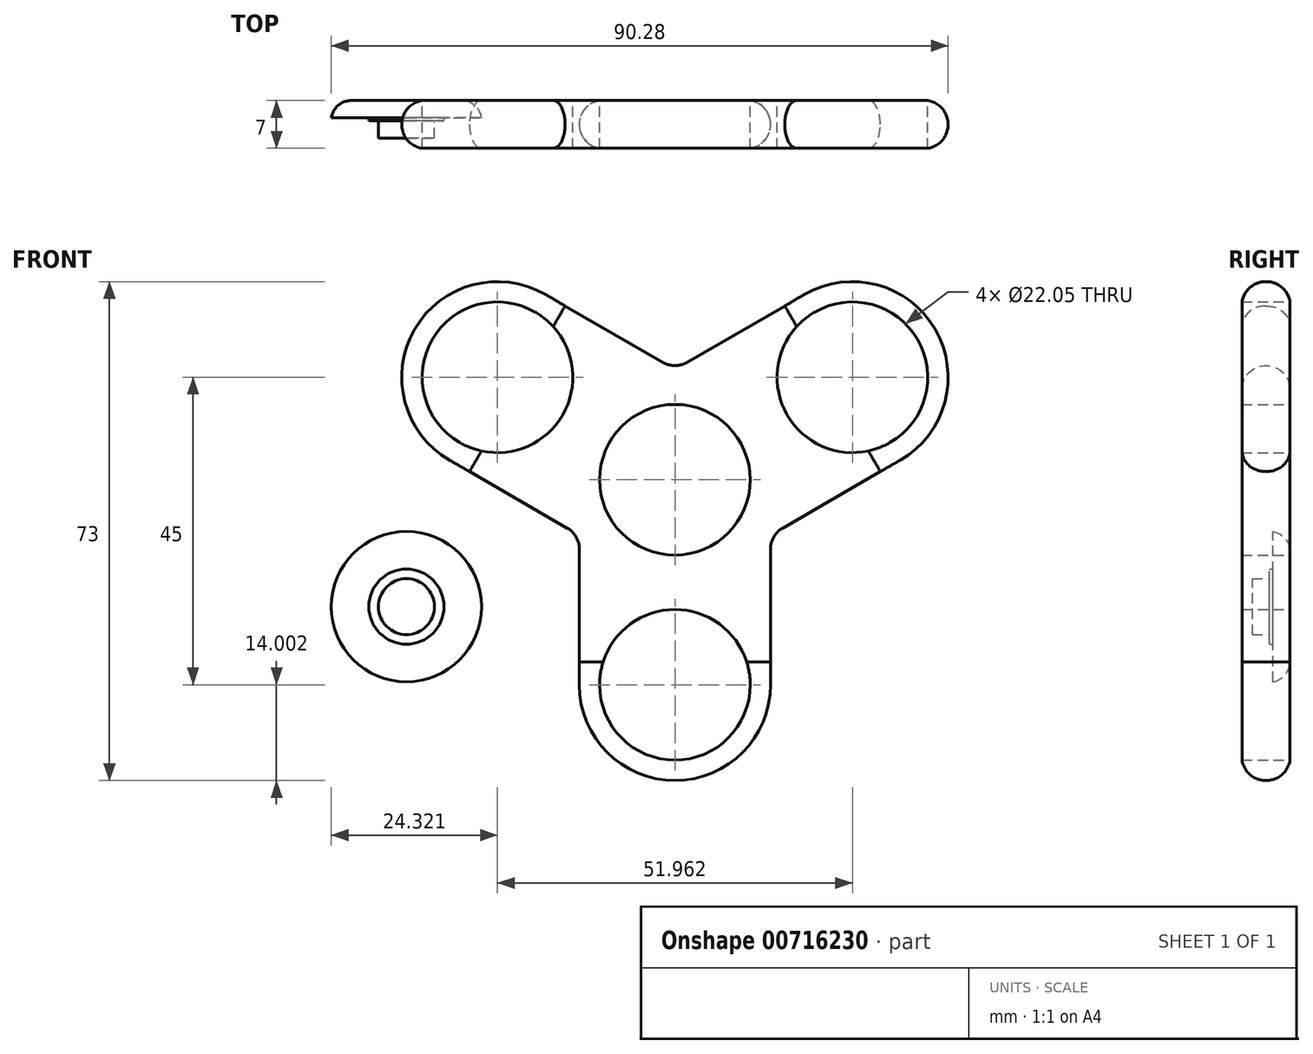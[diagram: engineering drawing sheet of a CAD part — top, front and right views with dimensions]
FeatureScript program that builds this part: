
annotation { "Feature Type Name" : "Feature", "Feature Type Description" : "" }
export const myFeature = defineFeature(function(context is Context, id is Id, definition is map)
    precondition{}
    {
        {
            var Q0;
            Q0=qCreatedBy(makeId("Front.planeOp"),FACE);
            var sketch = newSketch(context, id + "F0", { "sketchPlane" : qUnion([Q0])});
            skLineSegment(sketch, "E0.bottom", {"start": v(-7.75, 14.35) * mm, "end": v(20.25, 14.35) * mm});
            skLineSegment(sketch, "E0.top", {"start": v(-7.75, -15.65) * mm, "end": v(20.25, -15.65) * mm});
            skLineSegment(sketch, "E0.left", {"start": v(-7.75, 14.35) * mm, "end": v(-7.75, -15.65) * mm});
            skLineSegment(sketch, "E0.right", {"start": v(20.25, 14.35) * mm, "end": v(20.25, -15.65) * mm});
            skCircle(sketch, "E1", {"center": v(6.25, 14.35) * mm, "radius": 14 * mm});
            skCircle(sketch, "E2", {"center": v(6.25, 14.35) * mm, "radius": 11.03 * mm});
            skCircle(sketch, "E3", {"center": v(6.25, -15.65) * mm, "radius": 14 * mm});
            skCircle(sketch, "E4", {"center": v(6.25, -15.65) * mm, "radius": 11.03 * mm});
            skSolve(sketch);
        }
        {
            var Q0;
            {var subQ1=sQuery(id+"F0.wireOp",EDGE,"E0.bottom");var subQ3=sQuery(id+"F0.wireOp",EDGE,"E2");var subQ4=makeQuery(id+"F0.imprint","INTERSECT",VERTEX,{"disambiguationData":[OD(0.0)],"derivedFrom":[subQ1,subQ3]});Q0=makeQuery(id+"F0.imprint","IMPRINT",FACE,{"disambiguationData":[TD([[makeQuery(id+"F0.imprint","IMPRINT",EDGE,{"disambiguationData":[TD([[subQ4,1.0]])],"derivedFrom":subQ3}),-1.0]])]});}
            var Q1;
            {var subQ1=sQuery(id+"F0.wireOp",EDGE,"E0.top");var subQ3=sQuery(id+"F0.wireOp",EDGE,"E4");var subQ4=makeQuery(id+"F0.imprint","INTERSECT",VERTEX,{"disambiguationData":[OD(0.0)],"derivedFrom":[subQ1,subQ3]});Q1=makeQuery(id+"F0.imprint","IMPRINT",FACE,{"disambiguationData":[TD([[makeQuery(id+"F0.imprint","IMPRINT",EDGE,{"disambiguationData":[TD([[subQ4,-1.0]])],"derivedFrom":subQ3}),-1.0]])]});}
            var Q2;
            {var subQ1=sQuery(id+"F0.wireOp",EDGE,"E0.bottom");var subQ3=sQuery(id+"F0.wireOp",EDGE,"E2");var subQ4=makeQuery(id+"F0.imprint","INTERSECT",VERTEX,{"disambiguationData":[OD(0.0)],"derivedFrom":[subQ1,subQ3]});Q2=makeQuery(id+"F0.imprint","IMPRINT",FACE,{"disambiguationData":[TD([[makeQuery(id+"F0.imprint","IMPRINT",EDGE,{"disambiguationData":[TD([[subQ4,-1.0]])],"derivedFrom":subQ3}),-1.0]])]});}
            var Q3;
            {var subQ1=sQuery(id+"F0.wireOp",EDGE,"E0.top");var subQ3=sQuery(id+"F0.wireOp",EDGE,"E4");var subQ4=makeQuery(id+"F0.imprint","INTERSECT",VERTEX,{"disambiguationData":[OD(0.0)],"derivedFrom":[subQ1,subQ3]});Q3=makeQuery(id+"F0.imprint","IMPRINT",FACE,{"disambiguationData":[TD([[makeQuery(id+"F0.imprint","IMPRINT",EDGE,{"disambiguationData":[TD([[subQ4,1.0]])],"derivedFrom":subQ3}),-1.0]])]});}
            var Q4;
            {var subQ0=sQuery(id+"F0.wireOp",EDGE,"E0.left");Q4=makeQuery(id+"F0.imprint","IMPRINT",FACE,{"disambiguationData":[TD([[makeQuery(id+"F0.imprint","IMPRINT",EDGE,{"derivedFrom":subQ0}),1.0]])]});}
            extrude(context, id + "F1", {"entities" : qUnion([Q0, Q1, Q2, Q3, Q4]), "depth" : 7 * mm, "offsetDistance" : 25 * mm});
        }
        {
            var Q0;
            Q0=makeQuery(id+"F1.opExtrude","SWEPT_BODY",BODY,{"disambiguationData":[OSD([sQuery(id+"F0.wireOp",EDGE,"E0.left"),sQuery(id+"F0.wireOp",EDGE,"E0.right"),sQuery(id+"F0.wireOp",EDGE,"E1"),sQuery(id+"F0.wireOp",EDGE,"E2"),sQuery(id+"F0.wireOp",EDGE,"E3"),sQuery(id+"F0.wireOp",EDGE,"E4")])]});
            var Q1;
            Q1=makeQuery(id+"F1.opExtrude","SWEPT_FACE",FACE,{"disambiguationData":[OSD([sQuery(id+"F0.wireOp",EDGE,"E1")])]});
            circularPattern(context, id + "F2", {"operationType" : NewBodyOperationType.ADD, "entities" : qUnion([Q0]), "axis" : qUnion([Q1]), "angle" : 360 * degree, "instanceCount" : 3, "equalSpace" : true});
        }
        {
            var Q0;
            Q0=qCreatedBy(makeId("Front.planeOp"),FACE);
            var sketch = newSketch(context, id + "F3", { "sketchPlane" : qUnion([Q0])});
            skCircle(sketch, "E5", {"center": v(-33.05, -4.22) * mm, "radius": 11 * mm});
            skCircle(sketch, "E6", {"center": v(-33.05, -4.22) * mm, "radius": 5.5 * mm});
            skCircle(sketch, "E7", {"center": v(-33.05, -4.22) * mm, "radius": 4.1 * mm});
            skSolve(sketch);
        }
        {
            var Q0;
            Q0 = qSketchRegion(id + "F3", true);
            extrude(context, id + "F4", {"entities" : qUnion([Q0]), "depth" : 2.5 * mm, "offsetDistance" : 25 * mm});
        }
        {
            var Q0;
            Q0=makeQuery(id+"F3.imprint","IMPRINT",FACE,{"disambiguationData":[TD([[makeQuery(id+"F3.imprint","IMPRINT",EDGE,{"derivedFrom":sQuery(id+"F3.wireOp",EDGE,"E6")}),1.0]])]});
            extrude(context, id + "F5", {"entities" : qUnion([Q0]), "operationType" : NewBodyOperationType.ADD, "depth" : 3 * mm, "offsetDistance" : 25 * mm});
        }
        {
            var Q0;
            Q0=makeQuery(id+"F3.imprint","IMPRINT",FACE,{"disambiguationData":[TD([[makeQuery(id+"F3.imprint","IMPRINT",EDGE,{"derivedFrom":sQuery(id+"F3.wireOp",EDGE,"E7")}),1.0]])]});
            extrude(context, id + "F6", {"entities" : qUnion([Q0]), "operationType" : NewBodyOperationType.ADD, "depth" : 5.5 * mm, "offsetDistance" : 25 * mm});
        }
        {
            var Q0;
            Q0=makeQuery(id+"F1.opExtrude","CAP_EDGE",EDGE,{"disambiguationData":[OSD([sQuery(id+"F0.wireOp",EDGE,"E0.right")])],"isStart":false});
            var Q1;
            Q1=makeQuery(id+"F2.opPattern","COPY",EDGE,{"derivedFrom":makeQuery(id+"F1.opExtrude","CAP_EDGE",EDGE,{"disambiguationData":[OSD([sQuery(id+"F0.wireOp",EDGE,"E0.right")])],"isStart":false}),"instanceName":"1"});
            var Q2;
            Q2=makeQuery(id+"F2.opPattern","COPY",EDGE,{"derivedFrom":makeQuery(id+"F1.opExtrude","CAP_EDGE",EDGE,{"disambiguationData":[OSD([sQuery(id+"F0.wireOp",EDGE,"E0.right")])],"isStart":false}),"instanceName":"2"});
            var Q3;
            Q3=makeQuery(id+"F2.opPattern","COPY",EDGE,{"derivedFrom":makeQuery(id+"F1.opExtrude","CAP_EDGE",EDGE,{"disambiguationData":[OSD([sQuery(id+"F0.wireOp",EDGE,"E0.left")])],"isStart":true}),"instanceName":"2"});
            var Q4;
            Q4=makeQuery(id+"F2.opPattern","COPY",EDGE,{"derivedFrom":makeQuery(id+"F1.opExtrude","CAP_EDGE",EDGE,{"disambiguationData":[OSD([sQuery(id+"F0.wireOp",EDGE,"E0.left")])],"isStart":true}),"instanceName":"1"});
            var Q5;
            Q5=makeQuery(id+"F1.opExtrude","CAP_EDGE",EDGE,{"disambiguationData":[OSD([sQuery(id+"F0.wireOp",EDGE,"E0.left")])],"isStart":true});
            var Q6;
            Q6=makeQuery(id+"F2.boolean.opBoolean","INTERSECT",EDGE,{"derivedFrom":[makeQuery(id+"F1.opExtrude","SWEPT_FACE",FACE,{"disambiguationData":[OSD([sQuery(id+"F0.wireOp",EDGE,"E0.left")])]}),makeQuery(id+"F2.opPattern","COPY",FACE,{"derivedFrom":makeQuery(id+"F1.opExtrude","SWEPT_FACE",FACE,{"disambiguationData":[OSD([sQuery(id+"F0.wireOp",EDGE,"E0.right")])]}),"instanceName":"1"})]});
            var Q7;
            Q7=makeQuery(id+"F2.boolean.opBoolean","INTERSECT",EDGE,{"derivedFrom":[makeQuery(id+"F1.opExtrude","SWEPT_FACE",FACE,{"disambiguationData":[OSD([sQuery(id+"F0.wireOp",EDGE,"E0.right")])]}),makeQuery(id+"F2.opPattern","COPY",FACE,{"derivedFrom":makeQuery(id+"F1.opExtrude","SWEPT_FACE",FACE,{"disambiguationData":[OSD([sQuery(id+"F0.wireOp",EDGE,"E0.left")])]}),"instanceName":"2"})]});
            var Q8;
            Q8=makeQuery(id+"F2.boolean.opBoolean","INTERSECT",EDGE,{"derivedFrom":[makeQuery(id+"F2.opPattern","COPY",FACE,{"derivedFrom":makeQuery(id+"F1.opExtrude","SWEPT_FACE",FACE,{"disambiguationData":[OSD([sQuery(id+"F0.wireOp",EDGE,"E0.left")])]}),"instanceName":"1"}),makeQuery(id+"F2.opPattern","COPY",FACE,{"derivedFrom":makeQuery(id+"F1.opExtrude","SWEPT_FACE",FACE,{"disambiguationData":[OSD([sQuery(id+"F0.wireOp",EDGE,"E0.right")])]}),"instanceName":"2"})]});
            fillet(context, id + "F7", {"entities" : qUnion([Q0, Q1, Q2, Q3, Q4, Q5, Q6, Q7, Q8]), "radius" : 3.5 * mm, "tangentPropagation" : true, "allowEdgeOverflow" : false});
        }
        {
            var Q0;
            Q0=makeQuery(id+"F4.opExtrude","CAP_EDGE",EDGE,{"disambiguationData":[OSD([sQuery(id+"F3.wireOp",EDGE,"E5")])],"isStart":true});
            fillet(context, id + "F8", {"entities" : qUnion([Q0]), "radius" : 3 * mm, "tangentPropagation" : true, "allowEdgeOverflow" : false});
        }
    });
